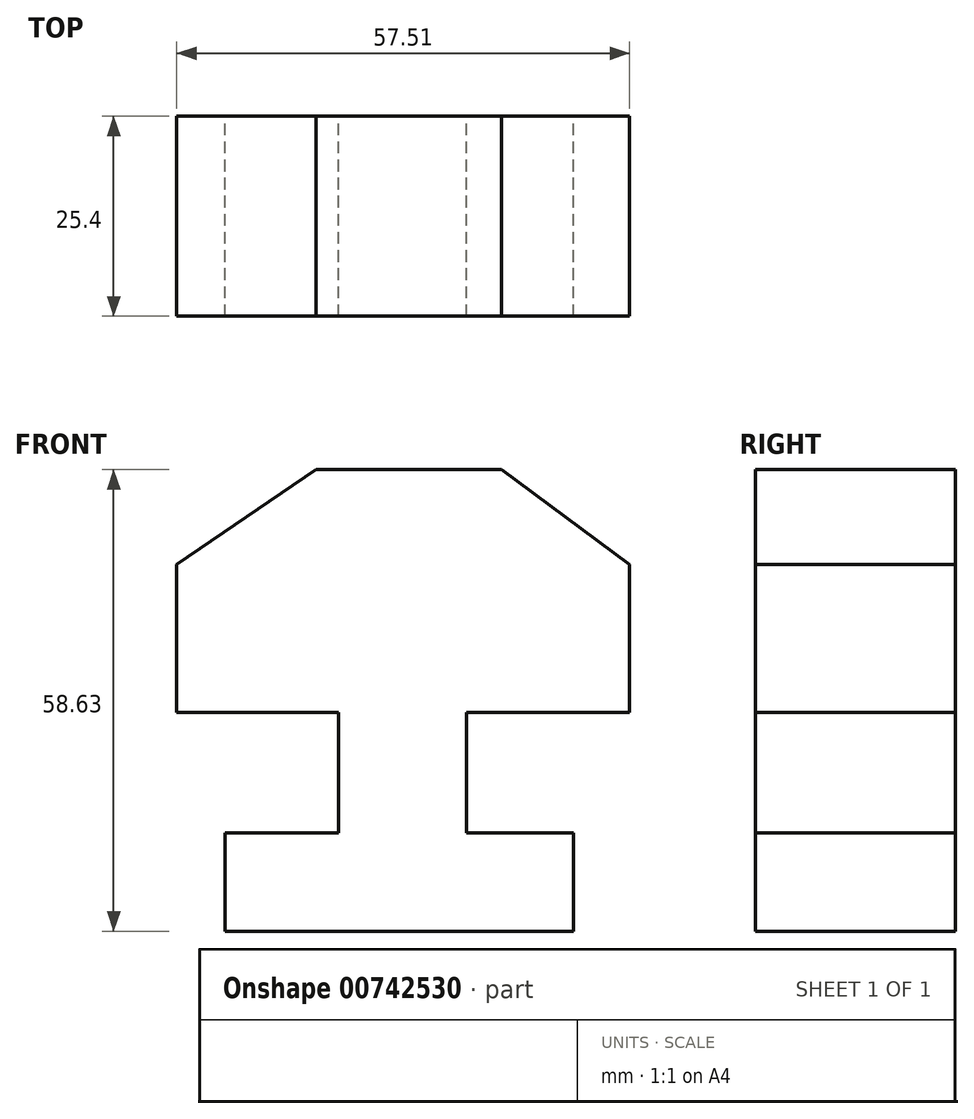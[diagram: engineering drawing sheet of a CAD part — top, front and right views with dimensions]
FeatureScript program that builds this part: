
annotation { "Feature Type Name" : "Feature", "Feature Type Description" : "" }
export const myFeature = defineFeature(function(context is Context, id is Id, definition is map)
    precondition{}
    {
        {
            var Q0;
            Q0=qCreatedBy(makeId("Front.planeOp"),FACE);
            var sketch = newSketch(context, id + "F0", { "sketchPlane" : qUnion([Q0])});
            skLineSegment(sketch, "E0", {"start": v(20.61, -55.73) * mm, "end": v(20.61, -43.21) * mm});
            skLineSegment(sketch, "E1", {"start": v(20.61, -43.21) * mm, "end": v(-23.67, -43.21) * mm});
            skLineSegment(sketch, "E2", {"start": v(-23.67, -43.21) * mm, "end": v(-23.67, -55.73) * mm});
            skLineSegment(sketch, "E3", {"start": v(-29.77, -27.94) * mm, "end": v(27.74, -27.94) * mm});
            skLineSegment(sketch, "E4", {"start": v(27.74, -27.94) * mm, "end": v(27.74, -9.1) * mm});
            skLineSegment(sketch, "E5", {"start": v(-29.77, -27.94) * mm, "end": v(-29.77, -9.1) * mm});
            skLineSegment(sketch, "E6", {"start": v(-29.77, -9.1) * mm, "end": v(-12.06, 2.9) * mm});
            skLineSegment(sketch, "E7", {"start": v(27.74, -9.1) * mm, "end": v(11.45, 2.9) * mm});
            skLineSegment(sketch, "E8", {"start": v(11.45, 2.9) * mm, "end": v(-12.06, 2.9) * mm});
            skLineSegment(sketch, "E9", {"start": v(-9.22, -43.21) * mm, "end": v(-9.22, -27.94) * mm});
            skLineSegment(sketch, "E10", {"start": v(7.02, -43.21) * mm, "end": v(7.02, -27.94) * mm});
            skLineSegment(sketch, "E11", {"start": v(-23.67, -55.73) * mm, "end": v(20.61, -55.73) * mm});
            skSolve(sketch);
        }
        {
            var Q0;
            {var subQ0=sQuery(id+"F0.wireOp",EDGE,"E4");Q0=makeQuery(id+"F0.imprint","IMPRINT",FACE,{"disambiguationData":[TD([[makeQuery(id+"F0.imprint","IMPRINT",EDGE,{"derivedFrom":subQ0}),1.0]])]});}
            var Q1;
            {var subQ0=sQuery(id+"F0.wireOp",EDGE,"E9");Q1=makeQuery(id+"F0.imprint","IMPRINT",FACE,{"disambiguationData":[TD([[makeQuery(id+"F0.imprint","IMPRINT",EDGE,{"derivedFrom":subQ0}),-1.0]])]});}
            var Q2;
            Q2=makeQuery(id+"F0.imprint","IMPRINT",FACE,{"disambiguationData":[TD([[makeQuery(id+"F0.imprint","IMPRINT",EDGE,{"derivedFrom":sQuery(id+"F0.wireOp",EDGE,"jeiFDz8p-J8CF-7J3F-Vur4-YxwdTCGTqGFT")}),1.0]])]});
            extrude(context, id + "F1", {"entities" : qUnion([Q0, Q1, Q2]), "depth" : 25.4 * mm, "offsetDistance" : 25.4 * mm});
        }
        {
            var Q0;
            {var subQ4=sQuery(id+"F0.wireOp",EDGE,"E0");Q0=makeQuery(id+"F0.imprint","IMPRINT",FACE,{"disambiguationData":[TD([[makeQuery(id+"F0.imprint","IMPRINT",EDGE,{"derivedFrom":subQ4}),1.0]])]});}
            extrude(context, id + "F2", {"entities" : qUnion([Q0]), "operationType" : NewBodyOperationType.ADD, "depth" : 25.4 * mm, "offsetDistance" : 25.4 * mm});
        }
    });
